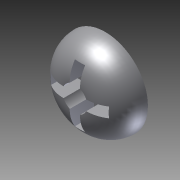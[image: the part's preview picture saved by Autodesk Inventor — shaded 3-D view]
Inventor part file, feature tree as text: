
AUTODESK INVENTOR PART (.ipt)
format: ipt  version: 2012 SP2 (Build 160219200, 219)  size: 143,872 bytes
history: native  units: in
note: dims shown in document units (in); Inventor stores cm internally (conversion verified against a paired STEP export)
features: extrude x2, sketch x2, fillet x1, reference x1
ambient origin geometry x8: Origin, YZ Plane, XZ Plane, XY Plane, X Axis, Y Axis, Z Axis, Center Point
bodies: Solid1 (feature_tree)
feature tree (6):
  extrude  "Extrusion1"  Depth=0.125in
  fillet  "Fillet1"  Radius=1.5748in
  extrude  "Extrusion2"  [1 undecoded]
  sketch  "Sketch1"  dims[d0=0.125in d1=0.0in d2=0.125in d3=1.5748in d5=360.0deg]
  reference  "Reference1"
  sketch  "Sketch2"  dims[d7=0.1in d8=0.0in]
note: 1 required parameter value undecoded (feature->parameter linkage not recoverable at this tier; creation-order binding heuristic only, values carry confidence <= 0.55)
